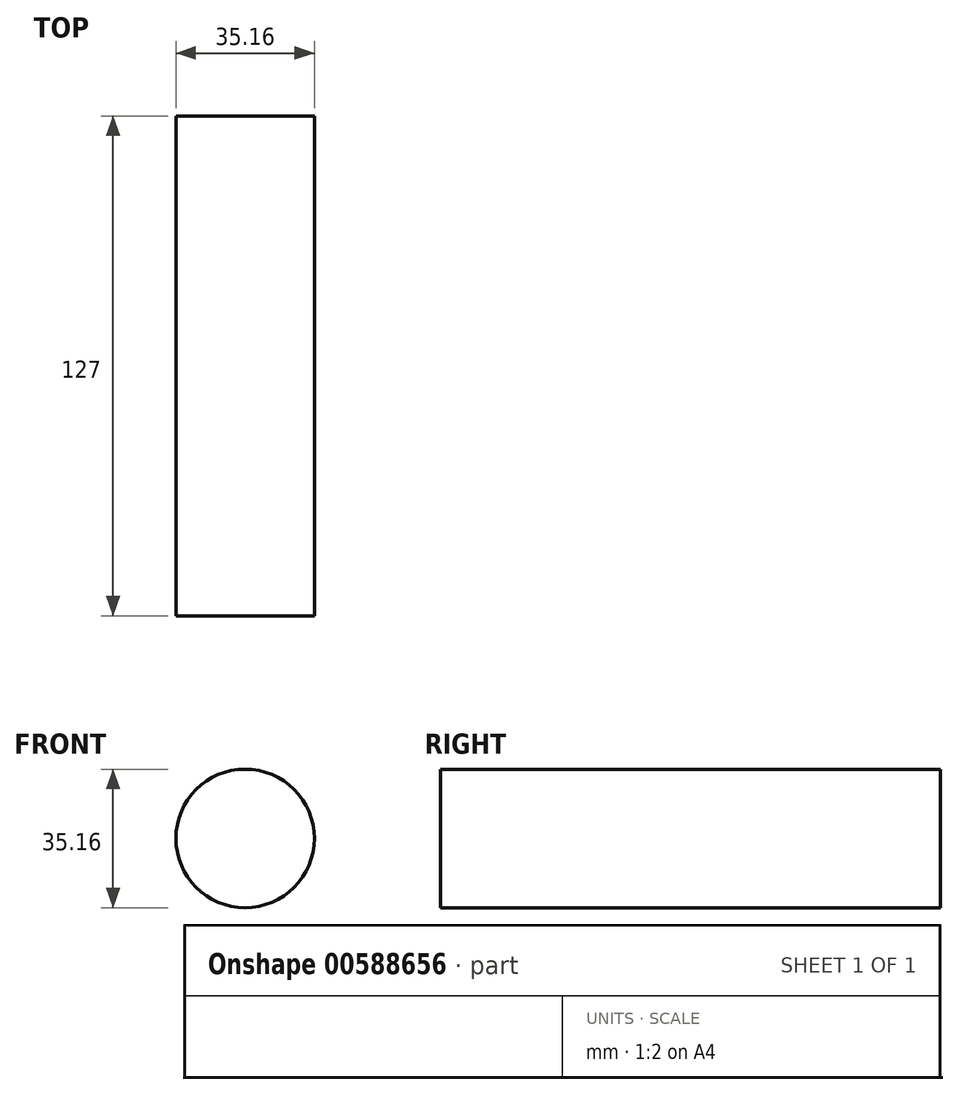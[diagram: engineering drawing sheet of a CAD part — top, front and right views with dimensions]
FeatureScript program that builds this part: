
annotation { "Feature Type Name" : "Feature", "Feature Type Description" : "" }
export const myFeature = defineFeature(function(context is Context, id is Id, definition is map)
    precondition{}
    {
        {
            var Q0;
            Q0=qCreatedBy(makeId("Front.planeOp"),FACE);
            var sketch = newSketch(context, id + "F0", { "sketchPlane" : qUnion([Q0])});
            skCircle(sketch, "E0", {"center": v(0, 0) * mm, "radius": 17.58 * mm});
            skSolve(sketch);
        }
        {
            var Q0;
            Q0=makeQuery(id+"F0.imprint","IMPRINT",FACE,{"disambiguationData":[TD([[makeQuery(id+"F0.imprint","IMPRINT",EDGE,{"derivedFrom":sQuery(id+"F0.wireOp",EDGE,"E0")}),1.0]])]});
            extrude(context, id + "F1", {"entities" : qUnion([Q0]), "depth" : 127 * mm, "offsetDistance" : 25.4 * mm});
        }
    });
